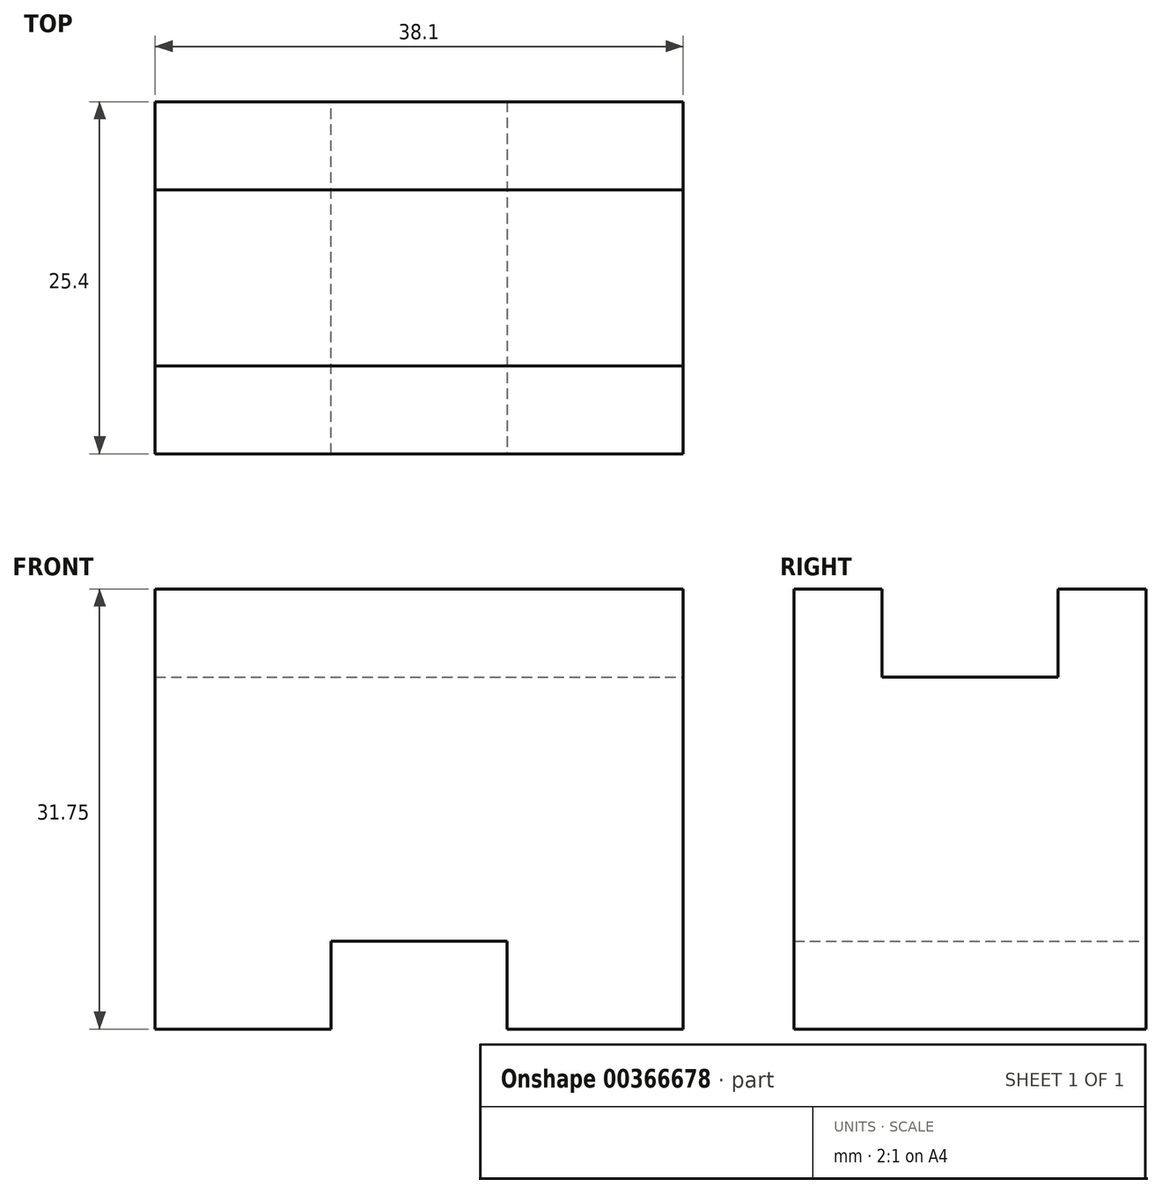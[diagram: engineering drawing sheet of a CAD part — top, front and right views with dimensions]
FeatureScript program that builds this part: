
annotation { "Feature Type Name" : "Feature", "Feature Type Description" : "" }
export const myFeature = defineFeature(function(context is Context, id is Id, definition is map)
    precondition{}
    {
        {
            var Q0;
            Q0=qCreatedBy(makeId("Front.planeOp"),FACE);
            var sketch = newSketch(context, id + "F0", { "sketchPlane" : qUnion([Q0])});
            skLineSegment(sketch, "E0", {"start": v(-47.95, 0) * mm, "end": v(-47.95, 31.75) * mm});
            skLineSegment(sketch, "E1", {"start": v(-47.95, 31.75) * mm, "end": v(-9.85, 31.75) * mm});
            skLineSegment(sketch, "E2", {"start": v(-9.85, 31.75) * mm, "end": v(-9.85, 0) * mm});
            skLineSegment(sketch, "E3", {"start": v(-9.85, 0) * mm, "end": v(-47.95, 0) * mm});
            skSolve(sketch);
        }
        {
            var Q0;
            Q0=makeQuery(id+"F0.imprint","IMPRINT",FACE,{"disambiguationData":[TD([[makeQuery(id+"F0.imprint","IMPRINT",EDGE,{"derivedFrom":sQuery(id+"F0.wireOp",EDGE,"E0")}),-1.0]])]});
            extrude(context, id + "F1", {"entities" : qUnion([Q0]), "depth" : 25.4 * mm});
        }
        {
            var Q0;
            Q0=makeQuery(id+"F1.opExtrude","SWEPT_FACE",FACE,{"disambiguationData":[OSD([sQuery(id+"F0.wireOp",EDGE,"E1")])]});
            var sketch = newSketch(context, id + "F2", { "sketchPlane" : qUnion([Q0])});
            skLineSegment(sketch, "E4", {"start": v(-47.95, -19.05) * mm, "end": v(-9.85, -19.05) * mm});
            skLineSegment(sketch, "E5", {"start": v(-9.85, -6.35) * mm, "end": v(-47.95, -6.35) * mm});
            skSolve(sketch);
        }
        {
            var Q0;
            {var subQ0=sQuery(id+"F2.wireOp",EDGE,"E4");Q0=makeQuery(id+"F2.imprint","IMPRINT",FACE,{"disambiguationData":[TD([[makeQuery(id+"F2.imprint","IMPRINT",EDGE,{"derivedFrom":subQ0}),1.0]])]});}
            extrude(context, id + "F3", {"entities" : qUnion([Q0]), "operationType" : NewBodyOperationType.REMOVE, "oppositeDirection" : true, "depth" : 6.35 * mm});
        }
        {
            var Q0;
            Q0=makeQuery(id+"F1.opExtrude","SWEPT_FACE",FACE,{"disambiguationData":[OSD([sQuery(id+"F0.wireOp",EDGE,"E3")])]});
            var sketch = newSketch(context, id + "F4", { "sketchPlane" : qUnion([Q0])});
            skLineSegment(sketch, "E6", {"start": v(-35.25, 25.4) * mm, "end": v(-35.25, 0) * mm});
            skLineSegment(sketch, "E7", {"start": v(-22.55, 0) * mm, "end": v(-22.55, 25.4) * mm});
            skSolve(sketch);
        }
        {
            var Q0;
            {var subQ0=sQuery(id+"F4.wireOp",EDGE,"E6");Q0=makeQuery(id+"F4.imprint","IMPRINT",FACE,{"disambiguationData":[TD([[makeQuery(id+"F4.imprint","IMPRINT",EDGE,{"derivedFrom":subQ0}),1.0]])]});}
            extrude(context, id + "F5", {"entities" : qUnion([Q0]), "operationType" : NewBodyOperationType.REMOVE, "oppositeDirection" : true, "depth" : 6.35 * mm});
        }
    });
